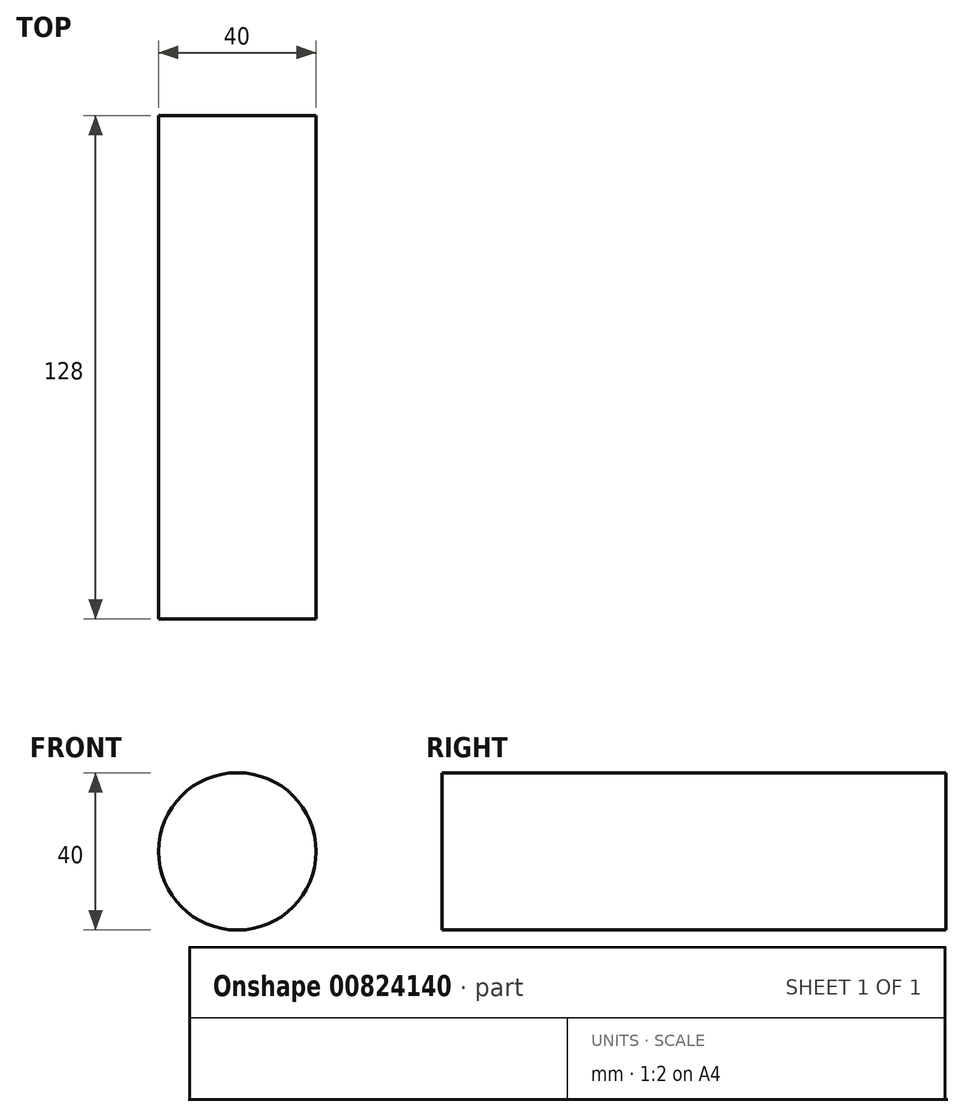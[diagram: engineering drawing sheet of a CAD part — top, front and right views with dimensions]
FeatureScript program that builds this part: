
annotation { "Feature Type Name" : "Feature", "Feature Type Description" : "" }
export const myFeature = defineFeature(function(context is Context, id is Id, definition is map)
    precondition{}
    {
        {
            var Q0;
            Q0=qCreatedBy(makeId("Front.planeOp"),FACE);
            var sketch = newSketch(context, id + "F0", { "sketchPlane" : qUnion([Q0])});
            skCircle(sketch, "E0", {"center": v(0, 0) * mm, "radius": 20 * mm});
            skSolve(sketch);
        }
        {
            var Q0;
            Q0=makeQuery(id+"F0.imprint","IMPRINT",FACE,{"disambiguationData":[TD([[makeQuery(id+"F0.imprint","IMPRINT",EDGE,{"derivedFrom":sQuery(id+"F0.wireOp",EDGE,"E0")}),1.0]])]});
            extrude(context, id + "F1", {"entities" : qUnion([Q0]), "depth" : 128 * mm, "offsetDistance" : 25 * mm});
        }
    });
